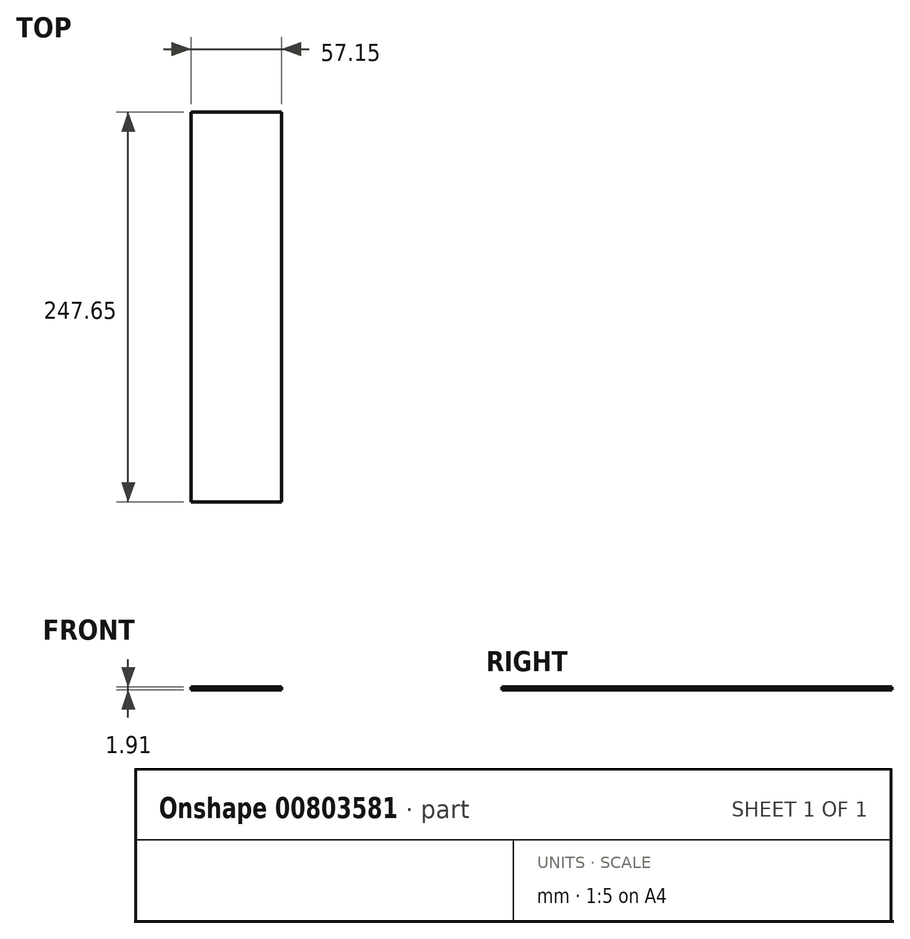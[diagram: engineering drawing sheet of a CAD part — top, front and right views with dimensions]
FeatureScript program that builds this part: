
annotation { "Feature Type Name" : "Feature", "Feature Type Description" : "" }
export const myFeature = defineFeature(function(context is Context, id is Id, definition is map)
    precondition{}
    {
        {
            var Q0;
            Q0=qCreatedBy(makeId("Top.planeOp"),FACE);
            var sketch = newSketch(context, id + "F0", { "sketchPlane" : qUnion([Q0])});
            skLineSegment(sketch, "E0.bottom", {"start": v(18.6, 88.13) * mm, "end": v(75.74, 88.13) * mm});
            skLineSegment(sketch, "E0.top", {"start": v(18.6, -159.52) * mm, "end": v(75.74, -159.52) * mm});
            skLineSegment(sketch, "E0.left", {"start": v(18.6, 88.13) * mm, "end": v(18.6, -159.52) * mm});
            skLineSegment(sketch, "E0.right", {"start": v(75.74, 88.13) * mm, "end": v(75.74, -159.52) * mm});
            skSolve(sketch);
        }
        {
            var Q0;
            Q0=makeQuery(id+"F0.imprint","IMPRINT",FACE,{"disambiguationData":[TD([[makeQuery(id+"F0.imprint","IMPRINT",EDGE,{"derivedFrom":sQuery(id+"F0.wireOp",EDGE,"E0.bottom")}),-1.0]])]});
            extrude(context, id + "F1", {"entities" : qUnion([Q0]), "depth" : 1.9 * mm, "offsetDistance" : 25.4 * mm});
        }
    });
